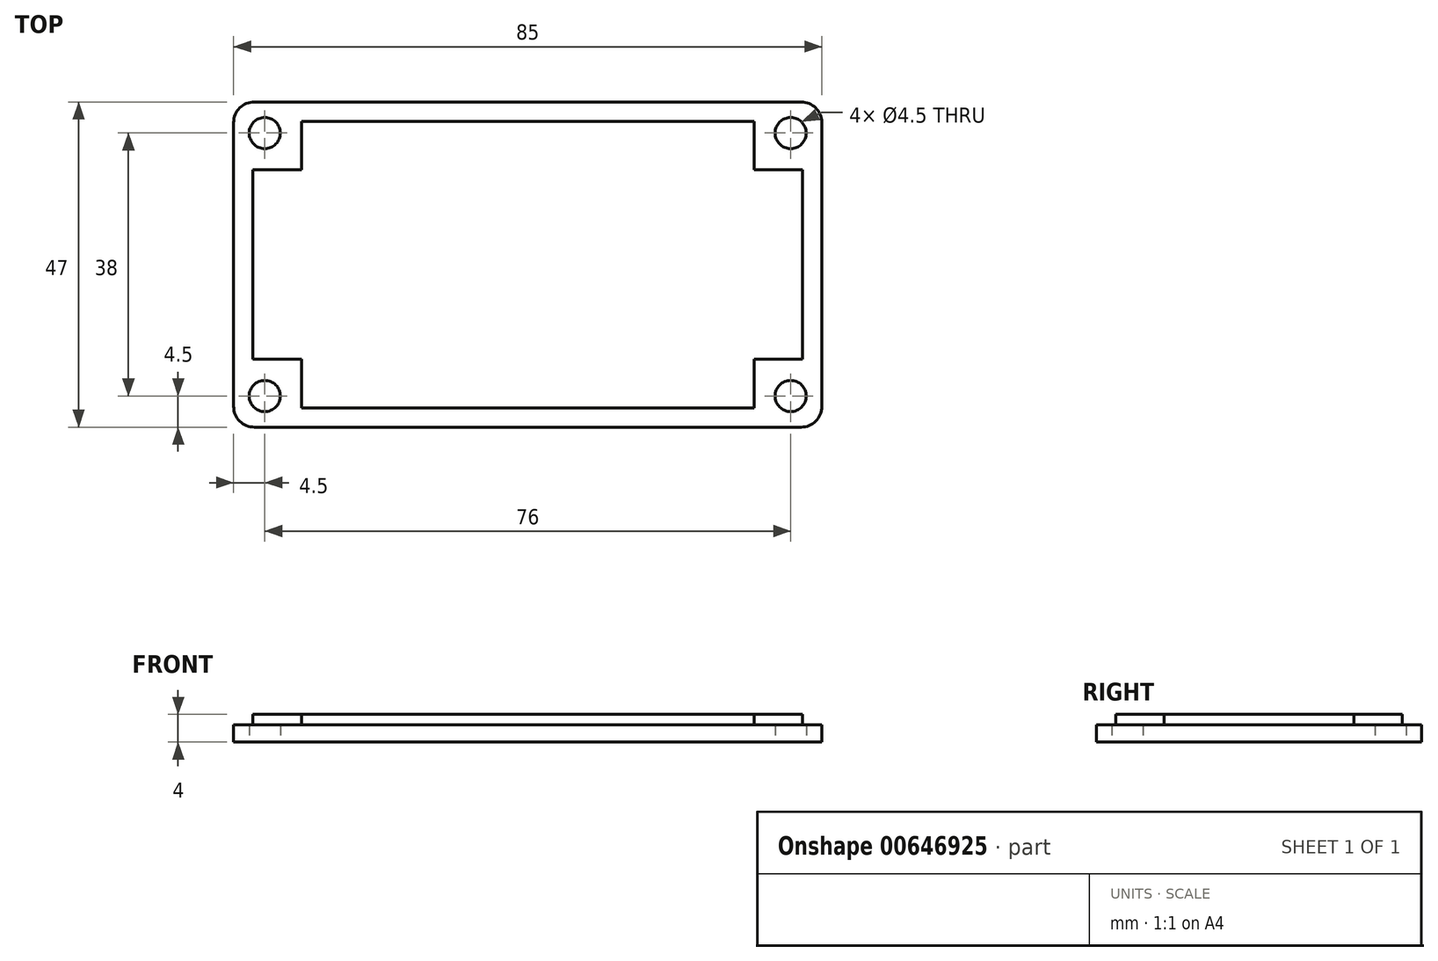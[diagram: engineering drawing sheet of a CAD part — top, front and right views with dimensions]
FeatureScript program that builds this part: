
annotation { "Feature Type Name" : "Feature", "Feature Type Description" : "" }
export const myFeature = defineFeature(function(context is Context, id is Id, definition is map)
    precondition{}
    {
        {
            var Q0;
            Q0=qCreatedBy(makeId("Top.planeOp"),FACE);
            var sketch = newSketch(context, id + "F0", { "sketchPlane" : qUnion([Q0])});
            skLineSegment(sketch, "E0.bottom", {"start": v(-39.5, 23.5) * mm, "end": v(39.5, 23.5) * mm});
            skLineSegment(sketch, "E0.top", {"start": v(-39.5, -23.5) * mm, "end": v(39.5, -23.5) * mm});
            skLineSegment(sketch, "E0.left", {"start": v(-42.5, 20.5) * mm, "end": v(-42.5, -20.5) * mm});
            skLineSegment(sketch, "E0.right", {"start": v(42.5, 20.5) * mm, "end": v(42.5, -20.5) * mm});
            skPoint(sketch, "E0.middle", {"position": v(0, 0) * mm});
            skCircle(sketch, "E1", {"center": v(-38, 19) * mm, "radius": 2.25 * mm});
            skCircle(sketch, "E2.MirrorC", {"center": v(38, 19) * mm, "radius": 2.25 * mm});
            skCircle(sketch, "E3.MirrorC", {"center": v(-38, -19) * mm, "radius": 2.25 * mm});
            skCircle(sketch, "E4.MirrorC", {"center": v(38, -19) * mm, "radius": 2.25 * mm});
            skPoint(sketch, "E5.visualSharp", {"position": v(42.5, 23.5) * mm});
            skArc(sketch, "E5.filletArc", {"start": v(42.5, 20.5) * mm, "mid": v(41.62, 22.62) * mm, "end": v(39.5, 23.5) * mm});
            skPoint(sketch, "E6.visualSharp", {"position": v(42.5, -23.5) * mm});
            skArc(sketch, "E6.filletArc", {"start": v(39.5, -23.5) * mm, "mid": v(41.62, -22.62) * mm, "end": v(42.5, -20.5) * mm});
            skPoint(sketch, "E7.visualSharp", {"position": v(-42.5, -23.5) * mm});
            skArc(sketch, "E7.filletArc", {"start": v(-42.5, -20.5) * mm, "mid": v(-41.62, -22.62) * mm, "end": v(-39.5, -23.5) * mm});
            skPoint(sketch, "E8.visualSharp", {"position": v(-42.5, 23.5) * mm});
            skArc(sketch, "E8.filletArc", {"start": v(-39.5, 23.5) * mm, "mid": v(-41.62, 22.62) * mm, "end": v(-42.5, 20.5) * mm});
            skSolve(sketch);
        }
        {
            var Q0;
            Q0=makeQuery(id+"F0.imprint","IMPRINT",FACE,{"disambiguationData":[TD([[makeQuery(id+"F0.imprint","IMPRINT",EDGE,{"derivedFrom":sQuery(id+"F0.wireOp",EDGE,"E0.bottom")}),-1.0]])]});
            extrude(context, id + "F1", {"entities" : qUnion([Q0]), "depth" : 2.5 * mm, "offsetDistance" : 25 * mm});
        }
        {
            var Q0;
            Q0=makeQuery(id+"F1.opExtrude","CAP_FACE",FACE,{"disambiguationData":[OSD([sQuery(id+"F0.wireOp",EDGE,"E0.bottom"),sQuery(id+"F0.wireOp",EDGE,"E0.top"),sQuery(id+"F0.wireOp",EDGE,"E0.left"),sQuery(id+"F0.wireOp",EDGE,"E0.right"),sQuery(id+"F0.wireOp",EDGE,"E1"),sQuery(id+"F0.wireOp",EDGE,"E2.MirrorC"),sQuery(id+"F0.wireOp",EDGE,"E3.MirrorC"),sQuery(id+"F0.wireOp",EDGE,"E4.MirrorC"),sQuery(id+"F0.wireOp",EDGE,"E5.filletArc"),sQuery(id+"F0.wireOp",EDGE,"E6.filletArc"),sQuery(id+"F0.wireOp",EDGE,"E7.filletArc"),sQuery(id+"F0.wireOp",EDGE,"E8.filletArc")])],"isStart":false});
            var sketch = newSketch(context, id + "F2", { "sketchPlane" : qUnion([Q0])});
            skLineSegment(sketch, "E9", {"start": v(-39.7, -13.7) * mm, "end": v(-32.7, -13.7) * mm});
            skLineSegment(sketch, "E10", {"start": v(-32.7, -13.7) * mm, "end": v(-32.7, -20.7) * mm});
            skLineSegment(sketch, "E11", {"start": v(-39.7, -13.7) * mm, "end": v(-39.7, 0) * mm});
            skLineSegment(sketch, "E12", {"start": v(-32.7, -20.7) * mm, "end": v(0, -20.7) * mm});
            skLineSegment(sketch, "E13.MirrorCS", {"start": v(32.7, -20.7) * mm, "end": v(0, -20.7) * mm});
            skLineSegment(sketch, "E14.MirrorCS", {"start": v(32.7, -13.7) * mm, "end": v(32.7, -20.7) * mm});
            skLineSegment(sketch, "E15.MirrorCS", {"start": v(39.7, -13.7) * mm, "end": v(32.7, -13.7) * mm});
            skLineSegment(sketch, "E16.MirrorCS", {"start": v(39.7, -13.7) * mm, "end": v(39.7, 0) * mm});
            skLineSegment(sketch, "E17.MirrorCS", {"start": v(39.7, 13.7) * mm, "end": v(39.7, 0) * mm});
            skLineSegment(sketch, "E18.MirrorCS", {"start": v(39.7, 13.7) * mm, "end": v(32.7, 13.7) * mm});
            skLineSegment(sketch, "E19.MirrorCS", {"start": v(32.7, 13.7) * mm, "end": v(32.7, 20.7) * mm});
            skLineSegment(sketch, "E20.MirrorCS", {"start": v(-32.7, 20.7) * mm, "end": v(0, 20.7) * mm});
            skLineSegment(sketch, "E21.MirrorCS", {"start": v(-32.7, 13.7) * mm, "end": v(-32.7, 20.7) * mm});
            skLineSegment(sketch, "E22.MirrorCS", {"start": v(-39.7, 13.7) * mm, "end": v(-32.7, 13.7) * mm});
            skLineSegment(sketch, "E23.MirrorCS", {"start": v(-39.7, 13.7) * mm, "end": v(-39.7, 0) * mm});
            skLineSegment(sketch, "E24.MirrorCS", {"start": v(32.7, 20.7) * mm, "end": v(0, 20.7) * mm});
            skSolve(sketch);
        }
        {
            var Q0;
            Q0 = qSketchRegion(id + "F2", true);
            extrude(context, id + "F3", {"entities" : qUnion([Q0]), "operationType" : NewBodyOperationType.ADD, "depth" : 1.5 * mm, "offsetDistance" : 25 * mm});
        }
    });
